# Revit family: Division_Twelve-Twigz-Seater_Café_Bench
name_source: partatom
category: Furniture
units: mm (PartAtom-declared; Revit-internal decimal feet)

## family parameters
Always vertical = Yes
Cut with Voids When Loaded = No
OmniClass Number = 23.40.20.00
OmniClass Title = General Furniture and Specialties
Room Calculation Point = No
Shared = No
Work Plane-Based = No

## types (8) — shared parameters
Assembly Code = E2020200
Default Elevation = 0"
Depth = 15"
Keynote = 12500
Low Emitting Finish = Yes
Low Emitting Material = Yes
Manufacturer = Division Twelve
Product Documentation Link = https://division12.com
Revit Model Built By = https://servex-us.com
Salvage or Reuse = Yes
Type Comments = Twigz
URL = https://division12.com
zero-valued in all types: Percentage of Recycled Content

## per-type parameters (varying)
| type | Description | Dist SL | Dist SR | Height | Support | T-1 | T-2 | T-3 | Width |
| 115103A | Two seater café bench with white oak seat | 2" | 0" | 17 1/2" | No | Yes | No | No | 42" |
| 115103B | Two seater café bench with upholstered seat | 2" | 0" | 18 1/2" | No | No | No | Yes | 42" |
| 115103C | Two seater café bench with steel seat | 2" | 0" | 17 1/4" | No | No | Yes | No | 42" |
| 115103F | Two seater café bench with stained oak seat | 2" | 0" | 17 1/2" | No | Yes | No | No | 42" |
| 115104A | Three seater café bench with white oak seat | 10 1/8" | 10 1/8" | 17 1/2" | Yes | Yes | No | No | 63" |
| 115104B | Three seater café bench with upholstered seat | 10 1/8" | 10 1/8" | 18 1/2" | Yes | No | No | Yes | 63" |
| 115104C | Three seater café bench with steel seat | 10 1/8" | 10 1/8" | 17 1/4" | Yes | No | Yes | No | 63" |
| 115104F | Three seater café bench with stained oak seat | 10 1/8" | 10 1/8" | 17 1/2" | Yes | Yes | No | No | 63" |

note: column(s) folded — value = type name in every type: Model

## geometry (parser evidence)
native form markers: Sweep x2
no freeform markers — native parametric forms only
